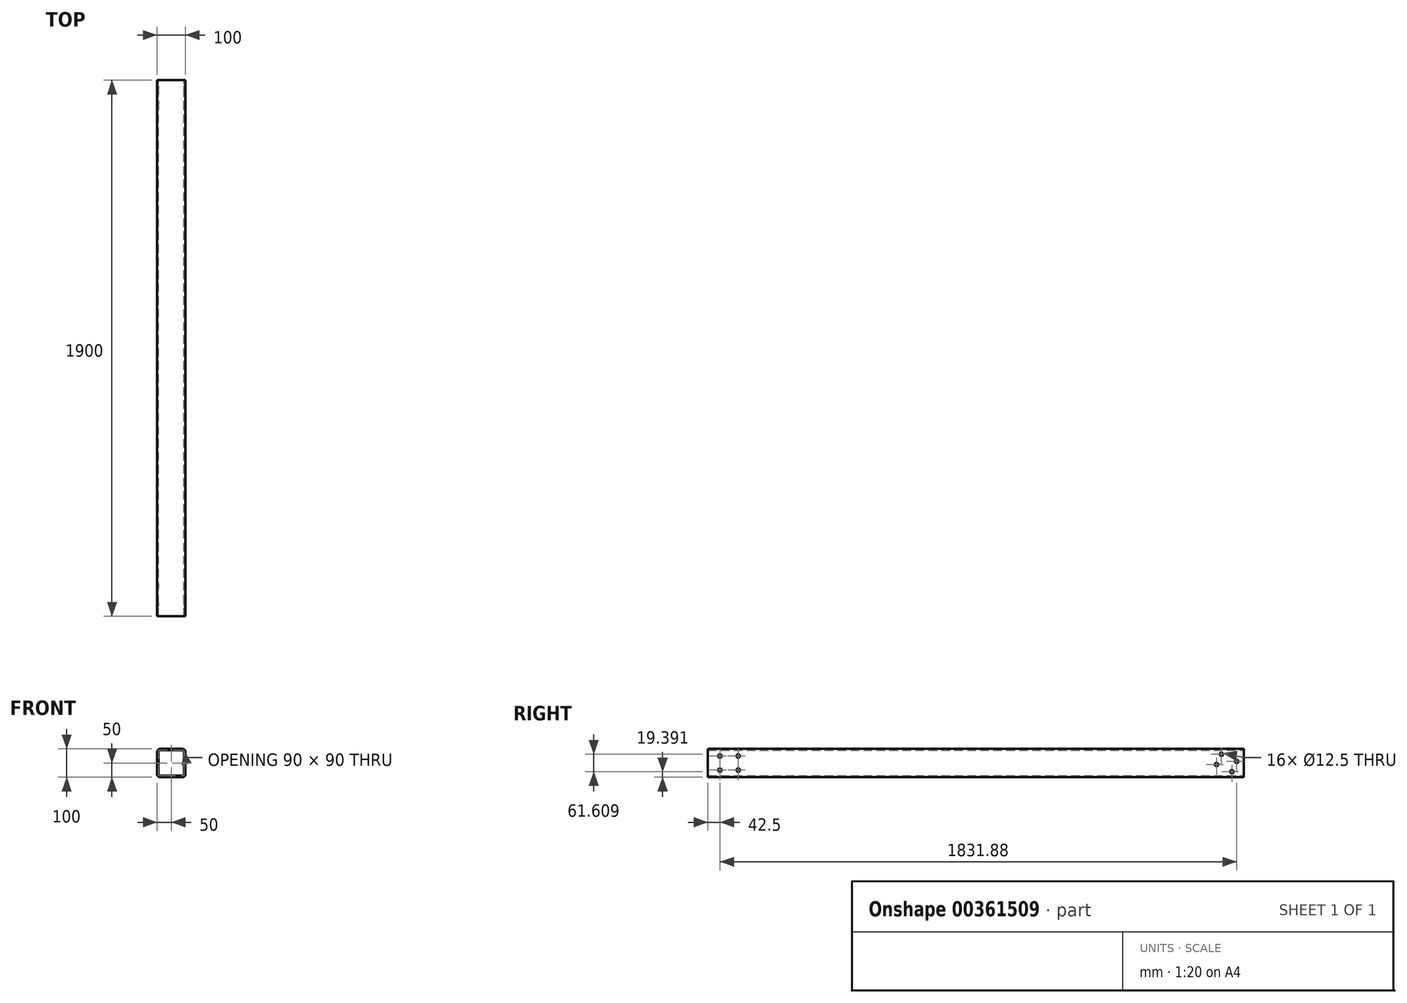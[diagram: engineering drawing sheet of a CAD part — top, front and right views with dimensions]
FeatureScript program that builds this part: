
annotation { "Feature Type Name" : "Feature", "Feature Type Description" : "" }
export const myFeature = defineFeature(function(context is Context, id is Id, definition is map)
    precondition{}
    {
        {
            var Q0;
            Q0=qCreatedBy(makeId("Front.planeOp"),FACE);
            var sketch = newSketch(context, id + "F0", { "sketchPlane" : qUnion([Q0])});
            skLineSegment(sketch, "E0.bottom", {"start": v(40, -50) * mm, "end": v(-40, -50) * mm});
            skLineSegment(sketch, "E0.top", {"start": v(40, 50) * mm, "end": v(-40, 50) * mm});
            skLineSegment(sketch, "E0.left", {"start": v(50, -40) * mm, "end": v(50, 40) * mm});
            skLineSegment(sketch, "E0.right", {"start": v(-50, -40) * mm, "end": v(-50, 40) * mm});
            skPoint(sketch, "E0.middle", {"position": v(0, 0) * mm});
            skPoint(sketch, "E1.visualSharp", {"position": v(-50, 50) * mm});
            skArc(sketch, "E1.filletArc", {"start": v(-40, 50) * mm, "mid": v(-47.07, 47.07) * mm, "end": v(-50, 40) * mm});
            skPoint(sketch, "E2.visualSharp", {"position": v(50, 50) * mm});
            skArc(sketch, "E2.filletArc", {"start": v(50, 40) * mm, "mid": v(47.07, 47.07) * mm, "end": v(40, 50) * mm});
            skPoint(sketch, "E3.visualSharp", {"position": v(50, -50) * mm});
            skArc(sketch, "E3.filletArc", {"start": v(40, -50) * mm, "mid": v(47.07, -47.07) * mm, "end": v(50, -40) * mm});
            skPoint(sketch, "E4.visualSharp", {"position": v(-50, -50) * mm});
            skArc(sketch, "E4.filletArc", {"start": v(-50, -40) * mm, "mid": v(-47.07, -47.07) * mm, "end": v(-40, -50) * mm});
            skArc(sketch, "E5.0", {"start": v(45, 40) * mm, "mid": v(43.54, 43.54) * mm, "end": v(40, 45) * mm});
            skLineSegment(sketch, "E5.1", {"start": v(45, -40) * mm, "end": v(45, 40) * mm});
            skLineSegment(sketch, "E5.2", {"start": v(40, 45) * mm, "end": v(-40, 45) * mm});
            skArc(sketch, "E5.3", {"start": v(40, -45) * mm, "mid": v(43.54, -43.54) * mm, "end": v(45, -40) * mm});
            skArc(sketch, "E5.4", {"start": v(-40, 45) * mm, "mid": v(-43.54, 43.54) * mm, "end": v(-45, 40) * mm});
            skLineSegment(sketch, "E5.5", {"start": v(-45, -40) * mm, "end": v(-45, 40) * mm});
            skArc(sketch, "E5.6", {"start": v(-45, -40) * mm, "mid": v(-43.54, -43.54) * mm, "end": v(-40, -45) * mm});
            skLineSegment(sketch, "E5.7", {"start": v(40, -45) * mm, "end": v(-40, -45) * mm});
            skSolve(sketch);
        }
        {
            var Q0;
            Q0 = qSketchRegion(id + "F0", true);
            extrude(context, id + "F1", {"entities" : qUnion([Q0]), "endBound" : BoundingType.SYMMETRIC, "depth" : 1900 * mm});
        }
        {
            var Q0;
            Q0=makeQuery(id+"F1.opExtrude","SWEPT_FACE",FACE,{"disambiguationData":[OSD([sQuery(id+"F0.wireOp",EDGE,"E0.left")])]});
            var sketch = newSketch(context, id + "F2", { "sketchPlane" : qUnion([Q0])});
            skLineSegment(sketch, "E6", {"start": v(-950, 0) * mm, "end": v(-875, 0) * mm, "construction": true});
            skLineSegment(sketch, "E7.bottom", {"start": v(-842.5, 25) * mm, "end": v(-907.5, 25) * mm, "construction": true});
            skLineSegment(sketch, "E7.top", {"start": v(-842.5, -25) * mm, "end": v(-907.5, -25) * mm, "construction": true});
            skLineSegment(sketch, "E7.left", {"start": v(-842.5, 25) * mm, "end": v(-842.5, -25) * mm, "construction": true});
            skLineSegment(sketch, "E7.right", {"start": v(-907.5, 25) * mm, "end": v(-907.5, -25) * mm, "construction": true});
            skPoint(sketch, "E7.middle", {"position": v(-875, 0) * mm});
            skCircle(sketch, "E8", {"center": v(-907.5, 25) * mm, "radius": 6.25 * mm});
            skCircle(sketch, "E9", {"center": v(-842.5, 25) * mm, "radius": 6.25 * mm});
            skCircle(sketch, "E10", {"center": v(-842.5, -25) * mm, "radius": 6.25 * mm});
            skCircle(sketch, "E11", {"center": v(-907.5, -25) * mm, "radius": 6.25 * mm});
            skSolve(sketch);
        }
        {
            var Q0;
            Q0 = qSketchRegion(id + "F2", true);
            extrude(context, id + "F3", {"entities" : qUnion([Q0]), "operationType" : NewBodyOperationType.REMOVE, "endBound" : BoundingType.THROUGH_ALL, "oppositeDirection" : true, "depth" : 25 * mm});
        }
        {
            var Q0;
            Q0=makeQuery(id+"F1.opExtrude","SWEPT_FACE",FACE,{"disambiguationData":[OSD([sQuery(id+"F0.wireOp",EDGE,"E0.left")])]});
            var sketch = newSketch(context, id + "F4", { "sketchPlane" : qUnion([Q0])});
            skLineSegment(sketch, "E12", {"start": v(924.38, 5.64) * mm, "end": v(870, 31) * mm, "construction": true});
            skLineSegment(sketch, "E13", {"start": v(870, 31) * mm, "end": v(853.1, -5.25) * mm, "construction": true});
            skLineSegment(sketch, "E14", {"start": v(853.1, -5.25) * mm, "end": v(907.47, -30.6) * mm, "construction": true});
            skLineSegment(sketch, "E15", {"start": v(907.47, -30.6) * mm, "end": v(924.38, 5.64) * mm, "construction": true});
            skCircle(sketch, "E16", {"center": v(870, 31) * mm, "radius": 6.25 * mm});
            skCircle(sketch, "E17", {"center": v(924.38, 5.64) * mm, "radius": 6.25 * mm});
            skCircle(sketch, "E18", {"center": v(907.47, -30.6) * mm, "radius": 6.25 * mm});
            skCircle(sketch, "E19", {"center": v(853.1, -5.25) * mm, "radius": 6.25 * mm});
            skSolve(sketch);
        }
        {
            var Q0;
            Q0 = qSketchRegion(id + "F4", true);
            extrude(context, id + "F5", {"entities" : qUnion([Q0]), "operationType" : NewBodyOperationType.REMOVE, "endBound" : BoundingType.THROUGH_ALL, "oppositeDirection" : true, "depth" : 25 * mm});
        }
    });
